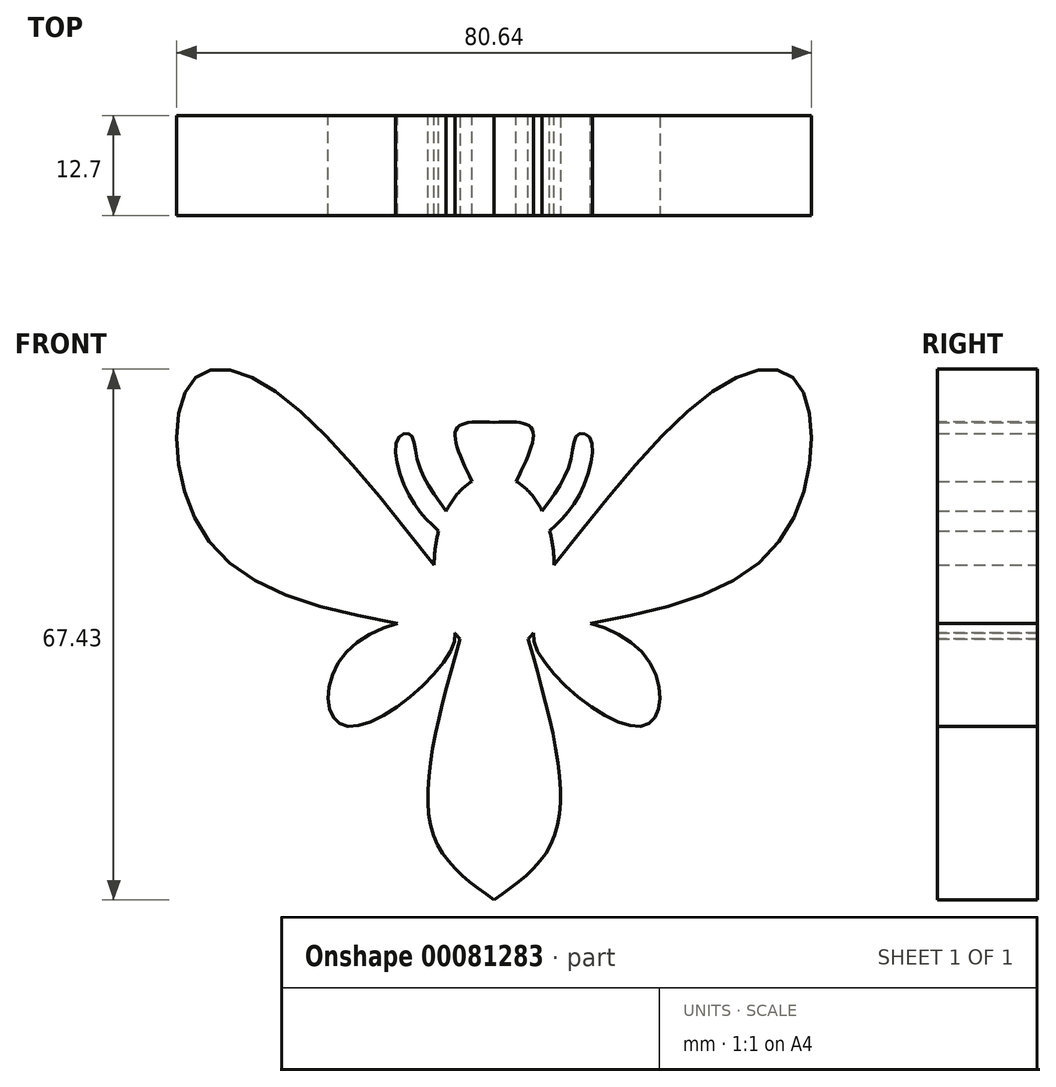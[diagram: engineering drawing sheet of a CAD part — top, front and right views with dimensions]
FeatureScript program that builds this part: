
annotation { "Feature Type Name" : "Feature", "Feature Type Description" : "" }
export const myFeature = defineFeature(function(context is Context, id is Id, definition is map)
    precondition{}
    {
        {
            var Q0;
            Q0=qCreatedBy(makeId("Front.planeOp"),FACE);
            var sketch = newSketch(context, id + "F0", { "sketchPlane" : qUnion([Q0])});
            skEllipticalArc(sketch, "E0", {});
            skFitSpline(sketch, "E1", {"points": [v(6.1, 20.13) * mm, v(9.65, 26.24) * mm, v(10.68, 29.84) * mm, v(12.22, 29.33) * mm, v(10.93, 22.38) * mm, v(7.06, 17.58) * mm], "startDerivative": vector(18.22, 24.8) * mm, "endDerivative": vector(-18.38, -17.5) * mm});
            skPoint(sketch, "E2.4.internal.snap0", {"position": v(7.62, 13.28) * mm});
            skFitSpline(sketch, "E2", {"points": [v(7.62, 13.28) * mm, v(29.2, 36.27) * mm, v(37.69, 37.3) * mm, v(40.26, 27.78) * mm, v(33.32, 13.28) * mm, v(5, 4.65) * mm], "startDerivative": vector(84.94, 107.88) * mm, "endDerivative": vector(-128.63, -20.6) * mm});
            skFitSpline(sketch, "E3", {"points": [v(5, 4.65) * mm, v(18.65, 2.32) * mm, v(18.65, -7.2) * mm, v(5, 4.65) * mm]});
            skFitSpline(sketch, "E4", {"points": [v(0, 31.39) * mm, v(4.76, 30.61) * mm, v(2.8, 23.9) * mm], "startDerivative": vector(13.66, 0.7) * mm, "endDerivative": vector(-7.36, -15.12) * mm});
            skFitSpline(sketch, "E5.MirrorCS", {"points": [v(0, 31.39) * mm, v(-4.76, 30.61) * mm, v(-2.8, 23.9) * mm], "startDerivative": vector(-13.66, 0.7) * mm, "endDerivative": vector(7.36, -15.12) * mm});
            skFitSpline(sketch, "E6.MirrorCS", {"points": [v(-6.1, 20.13) * mm, v(-9.65, 26.24) * mm, v(-10.68, 29.84) * mm, v(-12.22, 29.33) * mm, v(-10.93, 22.38) * mm, v(-7.06, 17.58) * mm], "startDerivative": vector(-18.22, 24.8) * mm, "endDerivative": vector(18.38, -17.5) * mm});
            skFitSpline(sketch, "E7.MirrorCS", {"points": [v(-7.62, 13.28) * mm, v(-29.2, 36.27) * mm, v(-37.69, 37.3) * mm, v(-40.26, 27.78) * mm, v(-33.32, 13.28) * mm, v(-5, 4.65) * mm], "startDerivative": vector(-84.94, 107.88) * mm, "endDerivative": vector(128.63, -20.6) * mm});
            skFitSpline(sketch, "E8.MirrorC", {"points": [v(-5, 4.65) * mm, v(-18.65, 2.32) * mm, v(-18.65, -7.2) * mm, v(-5, 4.65) * mm]});
            skPoint(sketch, "E9.MirrorCS.start.orphan", {"position": v(-2.07, 2.28) * mm});
            skFitSpline(sketch, "E10", {"points": [v(-4.32, 3.86) * mm, v(-7.85, -20.6) * mm, v(0, -29.27) * mm], "startDerivative": vector(-13.44, -47.22) * mm, "endDerivative": vector(24.4, -17.2) * mm});
            skFitSpline(sketch, "E11.MirrorCS", {"points": [v(4.32, 3.86) * mm, v(7.85, -20.6) * mm, v(0, -29.27) * mm], "startDerivative": vector(13.44, -47.22) * mm, "endDerivative": vector(-24.4, -17.2) * mm});
            const initialGuessF0  = {"E0": [0, 0.013276725989998408, 0, 1, 0.01143, 0.00762, 0.37745337081232394, 5.905731936367262]};
            skSetInitialGuess(sketch, initialGuessF0);
            skSolve(sketch);
        }
        {
            var Q0;
            Q0 = qSketchRegion(id + "F0", true);
            extrude(context, id + "F1", {"entities" : qUnion([Q0]), "depth" : 12.7 * mm});
        }
    });
